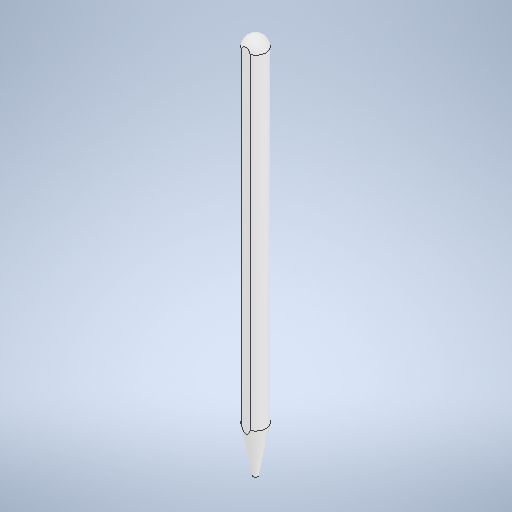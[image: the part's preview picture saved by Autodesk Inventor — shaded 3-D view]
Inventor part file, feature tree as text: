
AUTODESK INVENTOR PART (.ipt)
format: ipt  version: 2025.1 (Build 291241000, 241)  size: 283,648 bytes
history: native  units: mm
features: sketch x4, revolve x2, thicken_offset x2, extrude x1
ambient origin geometry x8: Origin, YZ Plane, XZ Plane, XY Plane, X Axis, Y Axis, Z Axis, Center Point
bodies: Solid1 (feature_tree)
feature tree (9):
  extrude  "Extrusion1"  Depth=140.0mm
  revolve  "Revolution4"  Angle=90.0deg
  thicken_offset  "Thicken7"
  revolve  "Revolution5"  [1 undecoded]
  thicken_offset  "Thicken8"
  sketch  "Sketch8"  dims[d31=20.0mm d33=20.0mm d38=90.0deg d39=3.0mm d40=2.0mm]
  sketch  "Sketch1"  dims[d2=140.0mm d3=0.0mm d26=0.4mm]
  sketch  "Sketch6"  dims[d27=9.1mm d28=90.0deg]
  sketch  "Sketch7"  dims[d29=2.0mm d30=2.0mm]
note: 1 required parameter value undecoded (feature->parameter linkage not recoverable at this tier; creation-order binding heuristic only, values carry confidence <= 0.55)
